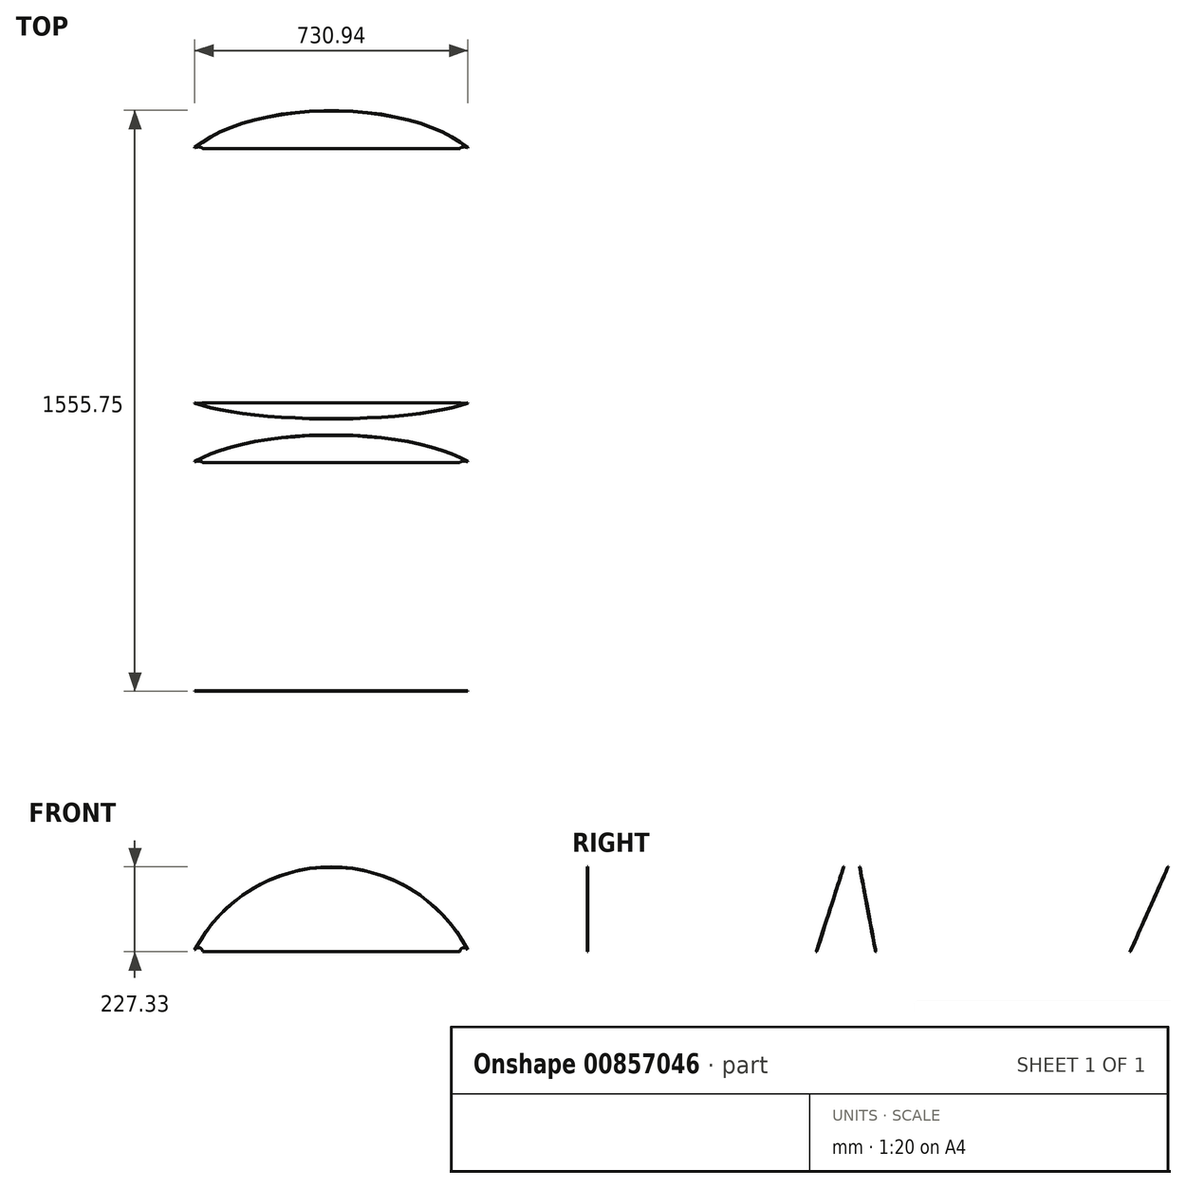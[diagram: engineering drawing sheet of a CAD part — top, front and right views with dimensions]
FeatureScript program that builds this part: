
annotation { "Feature Type Name" : "Feature", "Feature Type Description" : "" }
export const myFeature = defineFeature(function(context is Context, id is Id, definition is map)
    precondition{}
    {
        {
            var Q0;
            Q0=qCreatedBy(makeId("Front.planeOp"),FACE);
            var sketch = newSketch(context, id + "F0", { "sketchPlane" : qUnion([Q0])});
            skLineSegment(sketch, "E0", {"start": v(-355.6, 0) * mm, "end": v(355.6, 0) * mm});
            skCircle(sketch, "E1", {"center": v(-355.6, 0) * mm, "radius": 11.11 * mm});
            skCircle(sketch, "E2", {"center": v(355.6, 0) * mm, "radius": 11.11 * mm});
            skLineSegment(sketch, "E3", {"start": v(0, 0) * mm, "end": v(0, 227.33) * mm});
            skArc(sketch, "E4", {"start": v(365.47, 5.11) * mm, "mid": v(0, 227.33) * mm, "end": v(-365.47, 5.11) * mm});
            skSolve(sketch);
        }
        {
            var Q0;
            {var subQ0=sQuery(id+"F0.wireOp",EDGE,"E3");Q0=makeQuery(id+"F0.imprint","IMPRINT",FACE,{"disambiguationData":[TD([[makeQuery(id+"F0.imprint","IMPRINT",EDGE,{"derivedFrom":subQ0}),-1.0]])]});}
            var Q1;
            {var subQ0=sQuery(id+"F0.wireOp",EDGE,"E3");Q1=makeQuery(id+"F0.imprint","IMPRINT",FACE,{"disambiguationData":[TD([[makeQuery(id+"F0.imprint","IMPRINT",EDGE,{"derivedFrom":subQ0}),1.0]])]});}
            extrude(context, id + "F1", {"entities" : qUnion([Q0, Q1]), "depth" : 1555.75 * mm, "offsetDistance" : 25.4 * mm});
        }
        {
            var Q0;
            Q0=qCreatedBy(makeId("Right.planeOp"),FACE);
            var sketch = newSketch(context, id + "F2", { "sketchPlane" : qUnion([Q0])});
            skLineSegment(sketch, "E5.bottom", {"start": v(0, 0) * mm, "end": v(-1555.75, 0) * mm});
            skLineSegment(sketch, "E5.top", {"start": v(0, 227.33) * mm, "end": v(-1555.75, 227.33) * mm});
            skLineSegment(sketch, "E5.left", {"start": v(0, 0) * mm, "end": v(0, 227.33) * mm});
            skLineSegment(sketch, "E5.right", {"start": v(-1555.75, 0) * mm, "end": v(-1555.75, 227.33) * mm});
            skLineSegment(sketch, "E6", {"start": v(0, 227.33) * mm, "end": v(-101.6, 0) * mm});
            skLineSegment(sketch, "E7", {"start": v(-1.4, 227.33) * mm, "end": v(-103, 0) * mm});
            skLineSegment(sketch, "E8", {"start": v(-869.95, 227.33) * mm, "end": v(-942.98, 0) * mm});
            skLineSegment(sketch, "E9", {"start": v(-868.62, 227.33) * mm, "end": v(-941.64, 0) * mm});
            skLineSegment(sketch, "E10", {"start": v(-825.5, 227.33) * mm, "end": v(-782.64, 0) * mm});
            skLineSegment(sketch, "E11", {"start": v(-783.93, 0) * mm, "end": v(-826.8, 227.33) * mm});
            skLineSegment(sketch, "E12", {"start": v(-1554.48, 227.33) * mm, "end": v(-1554.48, 0) * mm});
            skSolve(sketch);
        }
        {
            var Q0;
            {var subQ0=sQuery(id+"F2.wireOp",EDGE,"E6");Q0=makeQuery(id+"F2.imprint","IMPRINT",FACE,{"disambiguationData":[TD([[makeQuery(id+"F2.imprint","IMPRINT",EDGE,{"derivedFrom":subQ0}),-1.0]])]});}
            var Q1;
            {var subQ0=sQuery(id+"F2.wireOp",EDGE,"E8");Q1=makeQuery(id+"F2.imprint","IMPRINT",FACE,{"disambiguationData":[TD([[makeQuery(id+"F2.imprint","IMPRINT",EDGE,{"derivedFrom":subQ0}),1.0]])]});}
            var Q2;
            {var subQ0=sQuery(id+"F2.wireOp",EDGE,"E10");Q2=makeQuery(id+"F2.imprint","IMPRINT",FACE,{"disambiguationData":[TD([[makeQuery(id+"F2.imprint","IMPRINT",EDGE,{"derivedFrom":subQ0}),-1.0]])]});}
            var Q3;
            {var subQ0=sQuery(id+"F2.wireOp",EDGE,"E5.right");Q3=makeQuery(id+"F2.imprint","IMPRINT",FACE,{"disambiguationData":[TD([[makeQuery(id+"F2.imprint","IMPRINT",EDGE,{"derivedFrom":subQ0}),-1.0]])]});}
            extrude(context, id + "F3", {"entities" : qUnion([Q0, Q1, Q2, Q3]), "operationType" : NewBodyOperationType.INTERSECT, "depth" : 762 * mm, "offsetDistance" : 25.4 * mm, "symmetric" : true});
        }
    });
